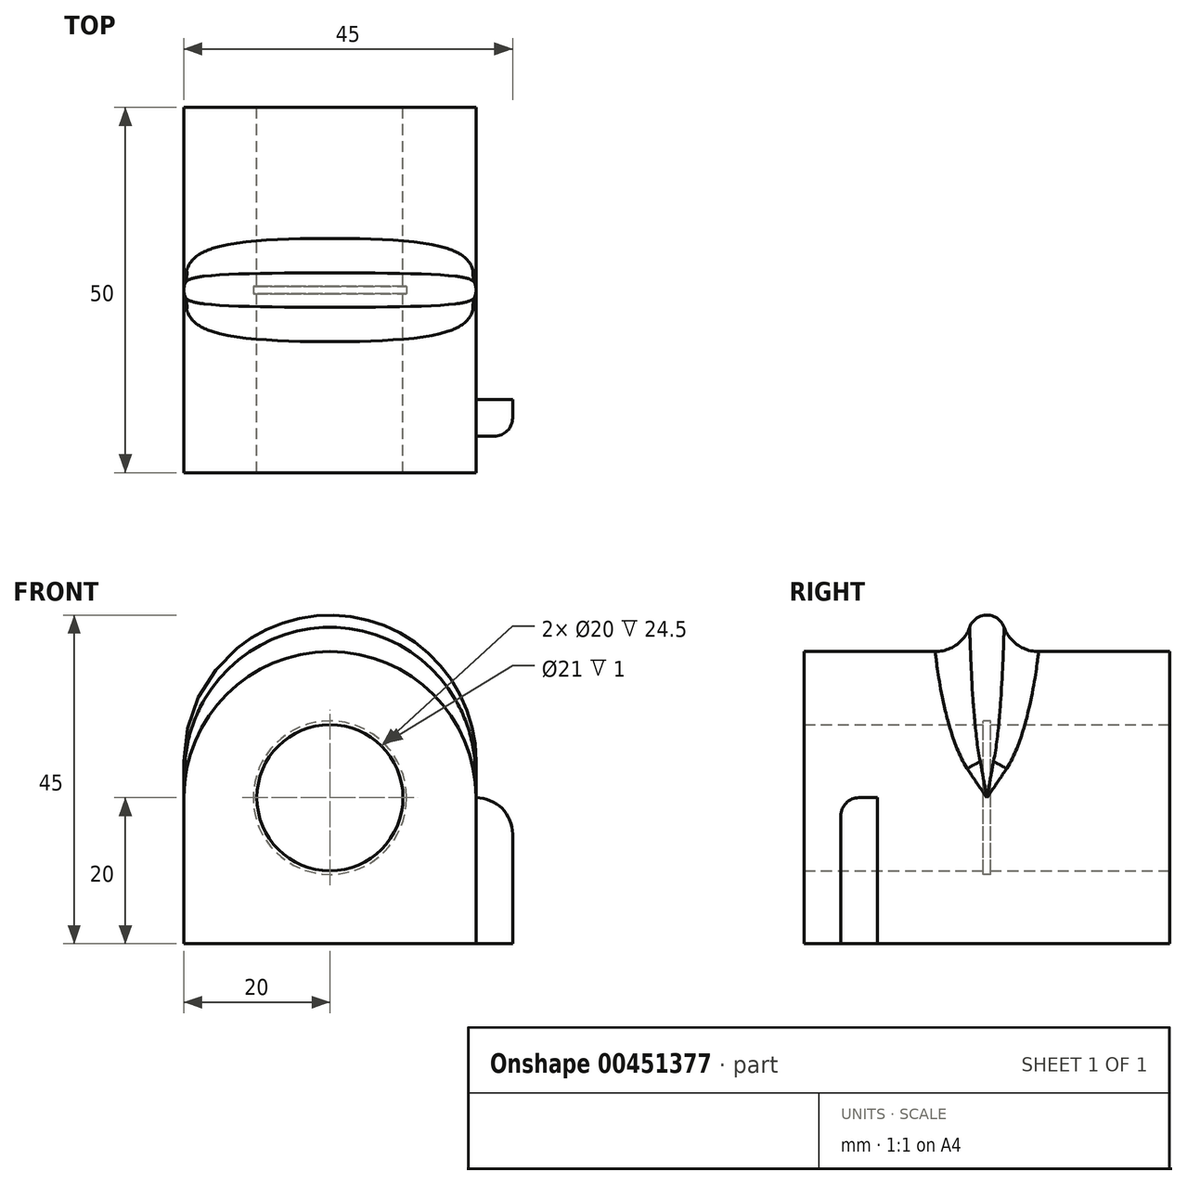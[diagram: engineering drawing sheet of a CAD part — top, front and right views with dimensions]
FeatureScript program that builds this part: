
annotation { "Feature Type Name" : "Feature", "Feature Type Description" : "" }
export const myFeature = defineFeature(function(context is Context, id is Id, definition is map)
    precondition{}
    {
        {
            var Q0;
            Q0=qCreatedBy(makeId("Front.planeOp"),FACE);
            var sketch = newSketch(context, id + "F0", { "sketchPlane" : qUnion([Q0])});
            skCircle(sketch, "E0", {"center": v(0, 0) * mm, "radius": 10 * mm});
            skLineSegment(sketch, "E1", {"start": v(-20, 0) * mm, "end": v(-20, -20) * mm});
            skLineSegment(sketch, "E2", {"start": v(20, 0) * mm, "end": v(20, -20) * mm});
            skArc(sketch, "E3", {"start": v(-20, 0) * mm, "mid": v(0, 20) * mm, "end": v(20, 0) * mm});
            skLineSegment(sketch, "E4", {"start": v(-20, -20) * mm, "end": v(25, -20) * mm});
            skLineSegment(sketch, "E5", {"start": v(-20, 0) * mm, "end": v(-20, 5) * mm});
            skLineSegment(sketch, "E6", {"start": v(0, 10) * mm, "end": v(0, 20) * mm});
            skLineSegment(sketch, "E7.MirrorCS", {"start": v(20, 0) * mm, "end": v(20, 5) * mm});
            skArc(sketch, "E8", {"start": v(-20, 5) * mm, "mid": v(0, 25) * mm, "end": v(20, 5) * mm});
            skLineSegment(sketch, "E9", {"start": v(25, -5) * mm, "end": v(25, -20) * mm});
            skArc(sketch, "E10", {"start": v(20, 0) * mm, "mid": v(23.54, -1.46) * mm, "end": v(25, -5) * mm});
            skPoint(sketch, "E11.orphan", {"position": v(25, 0) * mm});
            skCircle(sketch, "E12", {"center": v(0, 0) * mm, "radius": 10.5 * mm});
            skSolve(sketch);
        }
        {
            var Q0;
            {var subQ3=sQuery(id+"F0.wireOp",EDGE,"E1");Q0=makeQuery(id+"F0.imprint","IMPRINT",FACE,{"disambiguationData":[TD([[makeQuery(id+"F0.imprint","IMPRINT",EDGE,{"derivedFrom":subQ3}),1.0]])]});}
            var Q1;
            Q1=makeQuery(id+"F0.imprint","IMPRINT",FACE,{"disambiguationData":[TD([[makeQuery(id+"F0.imprint","IMPRINT",EDGE,{"derivedFrom":sQuery(id+"F0.wireOp",EDGE,"E0")}),-1.0]])]});
            extrude(context, id + "F1", {"entities" : qUnion([Q0, Q1]), "endBound" : BoundingType.SYMMETRIC, "depth" : 50 * mm});
        }
        {
            var Q0;
            Q0=makeQuery(id+"F0.imprint","IMPRINT",FACE,{"disambiguationData":[TD([[makeQuery(id+"F0.imprint","IMPRINT",EDGE,{"derivedFrom":sQuery(id+"F0.wireOp",EDGE,"E0")}),-1.0]])]});
            var Q1;
            Q1=sQuery(id+"F0.wireOp",EDGE,"E0");
            var Q2;
            Q2=sQuery(id+"F0.wireOp",EDGE,"E12");
            extrude(context, id + "F2", {"entities" : qUnion([Q0]), "operationType" : NewBodyOperationType.REMOVE, "surfaceEntities" : qUnion([Q1, Q2]), "endBound" : BoundingType.SYMMETRIC, "oppositeDirection" : true, "depth" : 1 * mm});
        }
        {
            var Q0;
            {var subQ0=sQuery(id+"F0.wireOp",EDGE,"E5");Q0=makeQuery(id+"F0.imprint","IMPRINT",FACE,{"disambiguationData":[TD([[makeQuery(id+"F0.imprint","IMPRINT",EDGE,{"derivedFrom":subQ0}),-1.0]])]});}
            extrude(context, id + "F3", {"entities" : qUnion([Q0]), "operationType" : NewBodyOperationType.ADD, "endBound" : BoundingType.SYMMETRIC, "depth" : 5 * mm});
        }
        {
            var Q0;
            {var subQ0=sQuery(id+"F0.wireOp",EDGE,"E2");Q0=makeQuery(id+"F0.imprint","IMPRINT",FACE,{"disambiguationData":[TD([[makeQuery(id+"F0.imprint","IMPRINT",EDGE,{"derivedFrom":subQ0}),1.0]])]});}
            extrude(context, id + "F4", {"entities" : qUnion([Q0]), "operationType" : NewBodyOperationType.ADD, "depth" : 20 * mm});
        }
        {
            var Q0;
            {var subQ0=sQuery(id+"F0.wireOp",EDGE,"E2");Q0=makeQuery(id+"F0.imprint","IMPRINT",FACE,{"disambiguationData":[TD([[makeQuery(id+"F0.imprint","IMPRINT",EDGE,{"derivedFrom":subQ0}),1.0]])]});}
            extrude(context, id + "F5", {"entities" : qUnion([Q0]), "operationType" : NewBodyOperationType.REMOVE, "depth" : 15 * mm});
        }
        {
            var Q0;
            Q0=makeQuery(id+"F3.opExtrude","CAP_EDGE",EDGE,{"disambiguationData":[OSD([sQuery(id+"F0.wireOp",EDGE,"E8")])],"isStart":false});
            var Q1;
            Q1=makeQuery(id+"F3.opExtrude","CAP_EDGE",EDGE,{"disambiguationData":[OSD([sQuery(id+"F0.wireOp",EDGE,"E8")])],"isStart":true});
            var Q2;
            Q2=makeQuery(id+"F5.boolean.opBoolean","COPY",EDGE,{"derivedFrom":makeQuery(id+"F5.opExtrude","CAP_EDGE",EDGE,{"disambiguationData":[OSD([sQuery(id+"F0.wireOp",EDGE,"E10")])],"isStart":false})});
            var Q3;
            Q3=makeQuery(id+"F4.opExtrude","CAP_EDGE",EDGE,{"disambiguationData":[OSD([sQuery(id+"F0.wireOp",EDGE,"E9")])],"isStart":false});
            fillet(context, id + "F6", {"entities" : qUnion([Q0, Q1, Q2, Q3]), "radius" : 2.5 * mm, "tangentPropagation" : true, "allowEdgeOverflow" : false});
        }
        {
            var Q0;
            Q0=makeQuery(id+"F3.opExtrude","CAP_EDGE",EDGE,{"disambiguationData":[OSD([sQuery(id+"F0.wireOp",EDGE,"E3")])],"isStart":false});
            var Q1;
            {var subQ0=sQuery(id+"F0.wireOp",EDGE,"E8");var subQ1=sQuery(id+"F0.wireOp",EDGE,"E7.MirrorCS");var subQ2=sQuery(id+"F0.wireOp",EDGE,"E5");var subQ3=sQuery(id+"F0.wireOp",EDGE,"E3");Q1=makeQuery(id+"F6.opFillet","BLEND_EDGE",EDGE,{"disambiguationData":[OD(1.0)],"blendedFrom":[makeQuery(id+"F3.opExtrude","CAP_EDGE",EDGE,{"disambiguationData":[OSD([subQ0])],"isStart":false}),makeQuery(id+"F3.boolean.opBoolean","SPLIT",FACE,{"disambiguationData":[TD([makeQuery(id+"F3.opExtrude","CAP_FACE",FACE,{"disambiguationData":[OSD([subQ3,subQ2,subQ1,subQ0])],"isStart":false})])],"derivedFrom":makeQuery(id+"F1.opExtrude","SWEPT_FACE",FACE,{"disambiguationData":[OSD([subQ3])]})})],"blendedInto":[makeQuery(id+"F3.boolean.opBoolean","SPLIT",FACE,{"disambiguationData":[TD([makeQuery(id+"F3.opExtrude","CAP_FACE",FACE,{"disambiguationData":[OSD([subQ3,subQ2,subQ1,subQ0])],"isStart":false})])],"derivedFrom":makeQuery(id+"F1.opExtrude","SWEPT_FACE",FACE,{"disambiguationData":[OSD([subQ3])]})})]});}
            var Q2;
            {var subQ0=sQuery(id+"F0.wireOp",EDGE,"E7.MirrorCS");var subQ1=sQuery(id+"F0.wireOp",EDGE,"E5");var subQ2=sQuery(id+"F0.wireOp",EDGE,"E3");Q2=makeQuery(id+"F6.opFillet","BLEND_EDGE",EDGE,{"blendedFrom":[makeQuery(id+"F3.opExtrude","CAP_EDGE",EDGE,{"disambiguationData":[OSD([subQ0])],"isStart":false}),makeQuery(id+"F3.boolean.opBoolean","SPLIT",FACE,{"disambiguationData":[TD([makeQuery(id+"F3.opExtrude","CAP_FACE",FACE,{"disambiguationData":[OSD([subQ2,subQ1,subQ0,sQuery(id+"F0.wireOp",EDGE,"E8")])],"isStart":false})])],"derivedFrom":makeQuery(id+"F1.opExtrude","SWEPT_FACE",FACE,{"disambiguationData":[OSD([subQ2])]})})],"blendedInto":[makeQuery(id+"F3.boolean.opBoolean","SPLIT",FACE,{"disambiguationData":[TD([makeQuery(id+"F3.opExtrude","CAP_FACE",FACE,{"disambiguationData":[OSD([subQ2,subQ1,subQ0,sQuery(id+"F0.wireOp",EDGE,"E8")])],"isStart":false})])],"derivedFrom":makeQuery(id+"F1.opExtrude","SWEPT_FACE",FACE,{"disambiguationData":[OSD([subQ2])]})})]});}
            var Q3;
            Q3=makeQuery(id+"F3.opExtrude","CAP_EDGE",EDGE,{"disambiguationData":[OSD([sQuery(id+"F0.wireOp",EDGE,"E3")])],"isStart":true});
            var Q4;
            Q4=makeQuery(id+"F4.opExtrude","CAP_EDGE",EDGE,{"disambiguationData":[OSD([sQuery(id+"F0.wireOp",EDGE,"E2")])],"isStart":false});
            fillet(context, id + "F7", {"entities" : qUnion([Q0, Q1, Q2, Q3, Q4]), "radius" : 5 * mm, "tangentPropagation" : true, "allowEdgeOverflow" : false});
        }
    });
